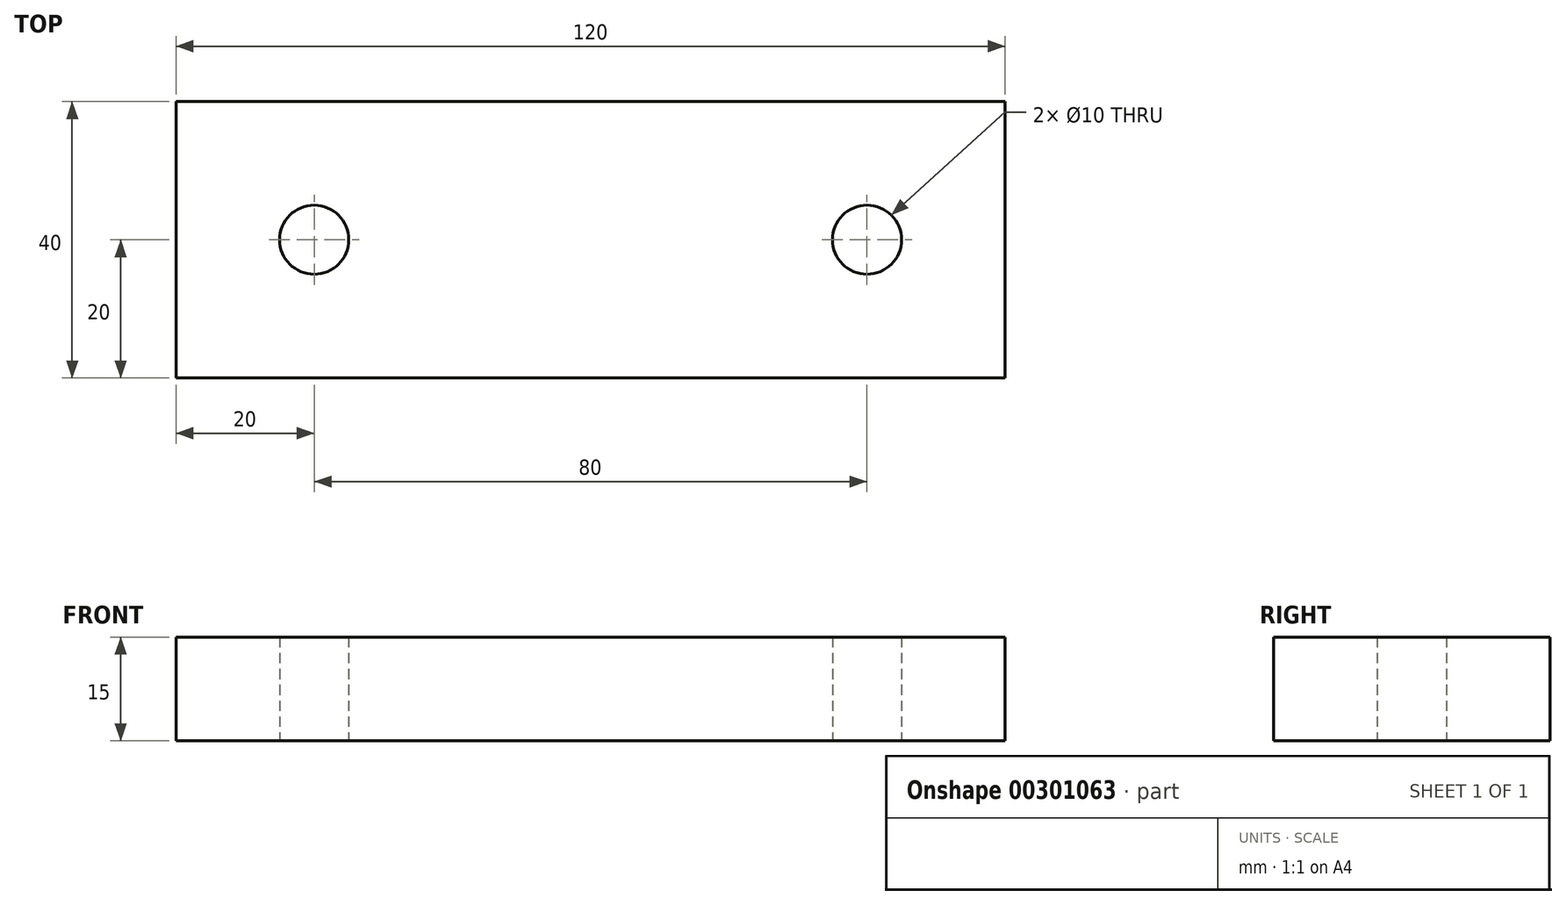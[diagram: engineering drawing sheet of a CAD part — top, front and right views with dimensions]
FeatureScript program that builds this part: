
annotation { "Feature Type Name" : "Feature", "Feature Type Description" : "" }
export const myFeature = defineFeature(function(context is Context, id is Id, definition is map)
    precondition{}
    {
        {
            var Q0;
            Q0=qCreatedBy(makeId("Top.planeOp"),FACE);
            var sketch = newSketch(context, id + "F0", { "sketchPlane" : qUnion([Q0])});
            skLineSegment(sketch, "E0.bottom", {"start": v(0, 0) * mm, "end": v(120, 0) * mm});
            skLineSegment(sketch, "E0.top", {"start": v(0, 40) * mm, "end": v(120, 40) * mm});
            skLineSegment(sketch, "E0.left", {"start": v(0, 0) * mm, "end": v(0, 40) * mm});
            skLineSegment(sketch, "E0.right", {"start": v(120, 0) * mm, "end": v(120, 40) * mm});
            skPoint(sketch, "E1", {"position": v(20, 40) * mm});
            skPoint(sketch, "E2", {"position": v(20, 20) * mm});
            skCircle(sketch, "E3", {"center": v(20, 20) * mm, "radius": 5 * mm});
            skPoint(sketch, "E4", {"position": v(100, 20) * mm});
            skCircle(sketch, "E5", {"center": v(100, 20) * mm, "radius": 5 * mm});
            skSolve(sketch);
        }
        {
            var Q0;
            Q0 = qSketchRegion(id + "F0", true);
            extrude(context, id + "F1", {"entities" : qUnion([Q0]), "depth" : 15 * mm});
        }
    });
